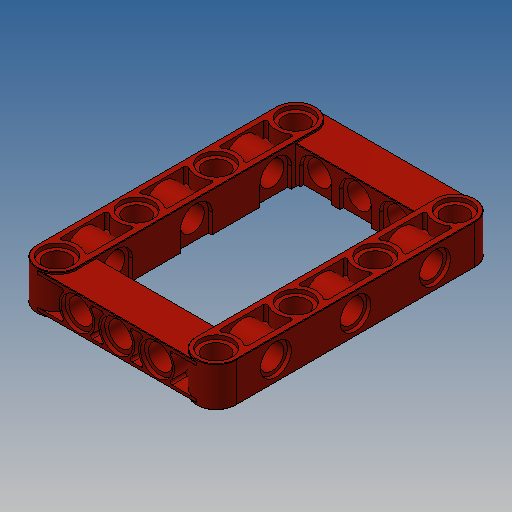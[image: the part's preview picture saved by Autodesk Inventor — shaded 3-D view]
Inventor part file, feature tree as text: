
AUTODESK INVENTOR PART (.ipt)
format: ipt  version: 2025 (Build 290162010, 162A)  size: 783,872 bytes
history: native  units: mm
features: extrude x13, sketch x9, mirror x3, fillet x2, projected_geometry x2, plane x1
ambient origin geometry x8: Origin, YZ Plane, XZ Plane, XY Plane, X Axis, Y Axis, Z Axis, Center Point
bodies: Solid1 (feature_tree)
feature tree (30):
  extrude  "Extrusion1"  Depth=0.8mm TaperAngle=0.0deg
  sketch  "Sketch6"  dims[d43=3.1mm d44=0.0mm d48=48.0mm]
  extrude  "Extrusion7"  Depth=3.1mm
  extrude  "Extrusion8"  Depth=4.8mm
  extrude  "Extrusion19"  Depth=0.4mm
  mirror  "Mirror5"
  sketch  "Sketch7"  dims[d49=6.4mm d50=4.8mm]
  extrude  "Extrusion9"  Depth=10.0mm
  extrude  "Extrusion10"  Depth=10.0mm TaperAngle=0.0deg
  extrude  "Extrusion11"  Depth=10.0mm
  extrude  "Extrusion18"  [1 undecoded]
  fillet  "Fillet2"  Radius=8.0mm
  plane  "Work Plane1"
  extrude  "Extrusion13"  Depth=5.8mm
  sketch  "Sketch12"  dims[d70=4.8mm d71=10.0mm d72=0.0mm]
  extrude  "Extrusion14"  Depth=3.1mm
  extrude  "Extrusion15"  Depth=3.1mm TaperAngle=0.0deg
  extrude  "Extrusion16"  Depth=3.1mm
  extrude  "Extrusion17"  Depth=3.1mm
  fillet  "Fillet3"  Radius=0.9mm
  mirror  "Mirror4"
  mirror  "Mirror3"
  projected_geometry  "Projected Loop4"
  sketch  "Skizze - Rechteckige Anordnung1"  dims[d14=8.0mm d15=0.0mm d41=0.8mm d42=0.0mm]
  sketch  "Sketch8"  dims[d51=16.0mm d60=0.4mm d61=0.1mm]
  sketch  "Sketch11"  dims[d62=30.0mm d64=16.0mm d65=10.0mm d67=10.0mm d69=7.2mm]
  projected_geometry  "Projected Loop5"
  sketch  "Sketch13"  dims[d73=10.0mm d74=0.0mm d75=6.2mm]
  sketch  "Sketch14"  dims[d76=0.8mm d77=0.0mm d78=-16.0mm d86=8.0mm]
  sketch  "Sketch15"  dims[d87=3.1mm d88=5.8mm d89=7.2mm d90=0.9mm d91=0.0mm d92=4.8mm d93=6.4mm d94=0.9mm d95=0.0mm d96=0.9mm d97=0.0mm d98=0.8mm d99=0.0mm d100=6.4mm d101=0.8mm d102=0.0mm d103=0.1mm d104=0.4mm d106=6.4mm d107=0.8mm d108=0.0mm d109=45.0deg d111=1.6mm d112=3.1mm d113=0.0mm d114=16.0mm d116=45.0deg d117=56.0mm d118=8.0mm]
note: 1 required parameter value undecoded (feature->parameter linkage not recoverable at this tier; creation-order binding heuristic only, values carry confidence <= 0.55)
